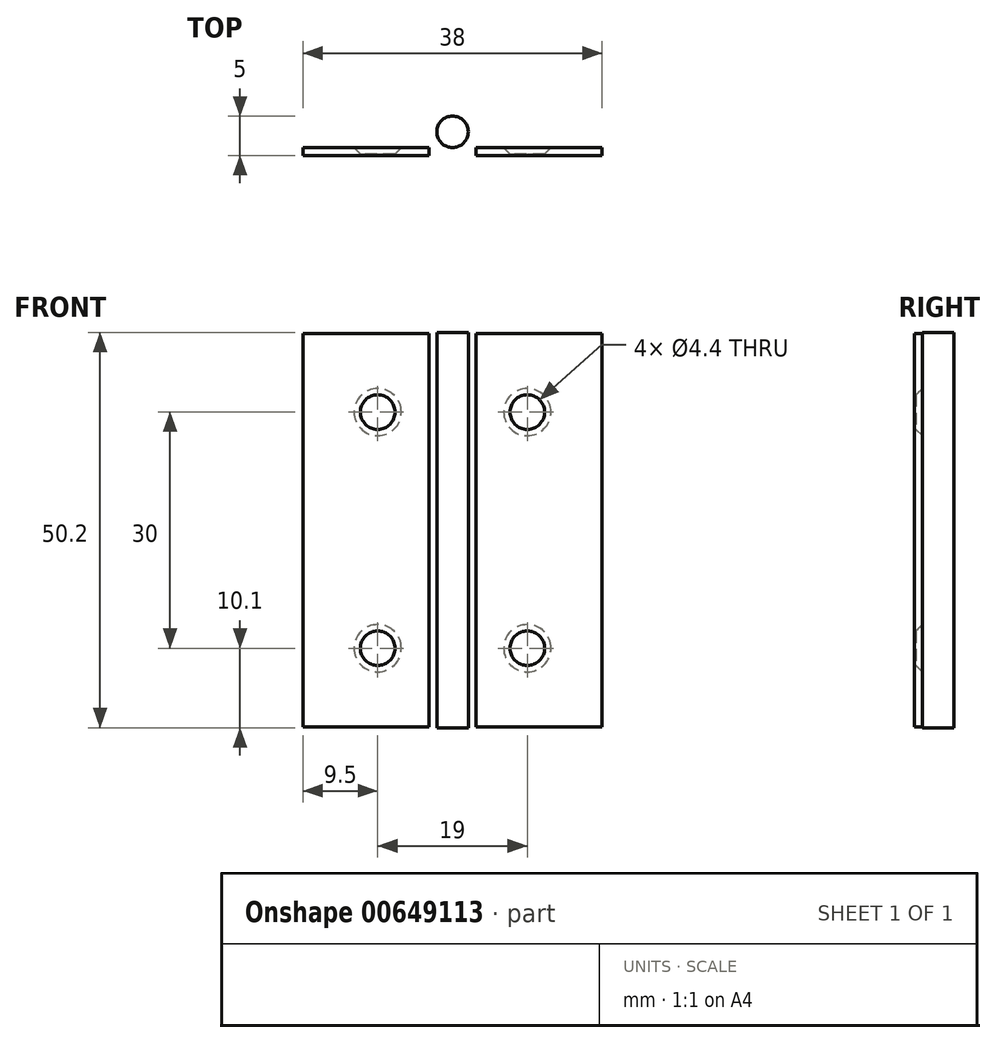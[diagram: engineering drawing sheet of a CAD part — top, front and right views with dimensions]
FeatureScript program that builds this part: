
annotation { "Feature Type Name" : "Feature", "Feature Type Description" : "" }
export const myFeature = defineFeature(function(context is Context, id is Id, definition is map)
    precondition{}
    {
        {
            var Q0;
            Q0=qCreatedBy(makeId("Top.planeOp"),FACE);
            var sketch = newSketch(context, id + "F0", { "sketchPlane" : qUnion([Q0])});
            skArc(sketch, "E0", {"start": v(0, -3) * mm, "mid": v(1.28, 2.71) * mm, "end": v(-2.32, -1.9) * mm});
            skLineSegment(sketch, "E1", {"start": v(0, -3) * mm, "end": v(-19, -3) * mm});
            skLineSegment(sketch, "E2", {"start": v(-19, -3) * mm, "end": v(-19, -2) * mm});
            skLineSegment(sketch, "E3", {"start": v(-19, -2) * mm, "end": v(0, -2) * mm});
            skArc(sketch, "E4.0", {"start": v(2.24, -2) * mm, "mid": v(0.07, 3) * mm, "end": v(-2.32, -1.9) * mm});
            skArc(sketch, "E5", {"start": v(0, -2) * mm, "mid": v(0.86, 1.8) * mm, "end": v(-1.55, -1.27) * mm});
            skLineSegment(sketch, "E6", {"start": v(-2.32, -1.9) * mm, "end": v(-1.55, -1.27) * mm});
            skSolve(sketch);
        }
        {
            var Q0;
            Q0=makeQuery(id+"F0.imprint","IMPRINT",FACE,{"disambiguationData":[TD([[makeQuery(id+"F0.imprint","IMPRINT",EDGE,{"derivedFrom":sQuery(id+"F0.wireOp",EDGE,"E0")}),1.0]])]});
            extrude(context, id + "F1", {"entities" : qUnion([Q0]), "oppositeDirection" : true, "depth" : 50 * mm, "offsetDistance" : 25 * mm});
        }
        {
            var Q0;
            Q0=qCreatedBy(makeId("Top.planeOp"),FACE);
            var sketch = newSketch(context, id + "F2", { "sketchPlane" : qUnion([Q0])});
            skLineSegment(sketch, "E7.MirrorCS", {"start": v(2.32, -1.9) * mm, "end": v(1.55, -1.27) * mm});
            skArc(sketch, "E8.MirrorCS", {"start": v(0, -2) * mm, "mid": v(-0.86, 1.8) * mm, "end": v(1.55, -1.27) * mm});
            skArc(sketch, "E9.MirrorCS", {"start": v(0, -3) * mm, "mid": v(-1.28, 2.71) * mm, "end": v(2.32, -1.9) * mm});
            skLineSegment(sketch, "E10.MirrorCS", {"start": v(19, -2) * mm, "end": v(0, -2) * mm});
            skLineSegment(sketch, "E11.MirrorCS", {"start": v(0, -3) * mm, "end": v(19, -3) * mm});
            skLineSegment(sketch, "E12.MirrorCS", {"start": v(19, -3) * mm, "end": v(19, -2) * mm});
            skSolve(sketch);
        }
        {
            var Q0;
            Q0=makeQuery(id+"F2.imprint","IMPRINT",FACE,{"disambiguationData":[TD([[makeQuery(id+"F2.imprint","IMPRINT",EDGE,{"derivedFrom":sQuery(id+"F2.wireOp",EDGE,"E7.MirrorCS")}),-1.0]])]});
            extrude(context, id + "F3", {"entities" : qUnion([Q0]), "oppositeDirection" : true, "depth" : 50 * mm, "offsetDistance" : 25 * mm});
        }
        {
            var Q0;
            Q0=qCreatedBy(makeId("Front.planeOp"),FACE);
            var sketch = newSketch(context, id + "F4", { "sketchPlane" : qUnion([Q0])});
            skLineSegment(sketch, "E13.bottom", {"start": v(-3, -50) * mm, "end": v(3, -50) * mm});
            skLineSegment(sketch, "E13.top", {"start": v(-3, -37.45) * mm, "end": v(3, -37.45) * mm});
            skLineSegment(sketch, "E13.left", {"start": v(-3, -50) * mm, "end": v(-3, -37.45) * mm});
            skLineSegment(sketch, "E13.right", {"start": v(3, -50) * mm, "end": v(3, -37.45) * mm});
            skLineSegment(sketch, "E14.0.1.0", {"start": v(3, -37.5) * mm, "end": v(3, -24.95) * mm});
            skLineSegment(sketch, "E14.0.1.1", {"start": v(-3, -37.5) * mm, "end": v(-3, -24.95) * mm});
            skLineSegment(sketch, "E14.0.1.2", {"start": v(-3, -24.95) * mm, "end": v(3, -24.95) * mm});
            skLineSegment(sketch, "E14.0.1.3", {"start": v(-3, -37.5) * mm, "end": v(3, -37.5) * mm});
            skLineSegment(sketch, "E14.0.2.0", {"start": v(3, -25) * mm, "end": v(3, -12.45) * mm});
            skLineSegment(sketch, "E14.0.2.1", {"start": v(-3, -25) * mm, "end": v(-3, -12.45) * mm});
            skLineSegment(sketch, "E14.0.2.2", {"start": v(-3, -12.45) * mm, "end": v(3, -12.45) * mm});
            skLineSegment(sketch, "E14.0.2.3", {"start": v(-3, -25) * mm, "end": v(3, -25) * mm});
            skLineSegment(sketch, "E14.0.3.0", {"start": v(3, -12.5) * mm, "end": v(3, 0.05) * mm});
            skLineSegment(sketch, "E14.0.3.1", {"start": v(-3, -12.5) * mm, "end": v(-3, 0.05) * mm});
            skLineSegment(sketch, "E14.0.3.2", {"start": v(-3, 0.05) * mm, "end": v(3, 0.05) * mm});
            skLineSegment(sketch, "E14.0.3.3", {"start": v(-3, -12.5) * mm, "end": v(3, -12.5) * mm});
            skLineSegment(sketch, "E14.direction1", {"start": v(-3, -50) * mm, "end": v(22, -50) * mm, "construction": true});
            skLineSegment(sketch, "E14.direction2", {"start": v(-3, -50) * mm, "end": v(-3, -37.5) * mm, "construction": true});
            skSolve(sketch);
        }
        {
            var Q0;
            Q0=makeQuery(id+"F4.imprint","IMPRINT",FACE,{"disambiguationData":[TD([[makeQuery(id+"F4.imprint","IMPRINT",EDGE,{"derivedFrom":sQuery(id+"F4.wireOp",EDGE,"E14.0.3.0")}),1.0]])]});
            var Q1;
            Q1=makeQuery(id+"F4.imprint","IMPRINT",FACE,{"disambiguationData":[TD([[makeQuery(id+"F4.imprint","IMPRINT",EDGE,{"derivedFrom":sQuery(id+"F4.wireOp",EDGE,"E14.0.1.0")}),1.0]])]});
            var Q2;
            {var subQ0=sQuery(id+"F4.wireOp",EDGE,"E14.0.1.2");Q2=makeQuery(id+"F4.imprint","IMPRINT",FACE,{"disambiguationData":[TD([[makeQuery(id+"F4.imprint","IMPRINT",EDGE,{"derivedFrom":subQ0}),-1.0]])]});}
            extrude(context, id + "F5", {"entities" : qUnion([Q0, Q1, Q2]), "operationType" : NewBodyOperationType.REMOVE, "endBound" : BoundingType.THROUGH_ALL, "oppositeDirection" : true, "depth" : 25 * mm, "offsetDistance" : 25 * mm, "hasSecondDirection" : true, "secondDirectionBound" : SecondDirectionBoundingType.THROUGH_ALL, "secondDirectionOppositeDirection" : false, "secondDirectionDepth" : 25 * mm});
        }
        {
            var Q0;
            Q0=makeQuery(id+"F4.imprint","IMPRINT",FACE,{"disambiguationData":[TD([[makeQuery(id+"F4.imprint","IMPRINT",EDGE,{"derivedFrom":sQuery(id+"F4.wireOp",EDGE,"E14.0.2.0")}),1.0]])]});
            var Q1;
            Q1=makeQuery(id+"F4.imprint","IMPRINT",FACE,{"disambiguationData":[TD([[makeQuery(id+"F4.imprint","IMPRINT",EDGE,{"derivedFrom":sQuery(id+"F4.wireOp",EDGE,"E13.bottom")}),1.0]])]});
            var Q2;
            {var subQ0=sQuery(id+"F4.wireOp",EDGE,"E14.0.2.2");Q2=makeQuery(id+"F4.imprint","IMPRINT",FACE,{"disambiguationData":[TD([[makeQuery(id+"F4.imprint","IMPRINT",EDGE,{"derivedFrom":subQ0}),-1.0]])]});}
            var Q3;
            {var subQ0=sQuery(id+"F4.wireOp",EDGE,"E13.top");Q3=makeQuery(id+"F4.imprint","IMPRINT",FACE,{"disambiguationData":[TD([[makeQuery(id+"F4.imprint","IMPRINT",EDGE,{"derivedFrom":subQ0}),-1.0]])]});}
            extrude(context, id + "F6", {"entities" : qUnion([Q0, Q1, Q2, Q3]), "operationType" : NewBodyOperationType.REMOVE, "endBound" : BoundingType.THROUGH_ALL, "oppositeDirection" : true, "depth" : 25 * mm, "offsetDistance" : 25 * mm, "hasSecondDirection" : true, "secondDirectionBound" : SecondDirectionBoundingType.THROUGH_ALL, "secondDirectionOppositeDirection" : false, "secondDirectionDepth" : 25 * mm});
        }
        {
            var Q0;
            Q0=qCreatedBy(makeId("Top.planeOp"),FACE);
            var sketch = newSketch(context, id + "F7", { "sketchPlane" : qUnion([Q0])});
            skCircle(sketch, "E15", {"center": v(0, 0) * mm, "radius": 2 * mm});
            skSolve(sketch);
        }
        {
            var Q0;
            Q0=makeQuery(id+"F7.imprint","IMPRINT",FACE,{"disambiguationData":[TD([[makeQuery(id+"F7.imprint","IMPRINT",EDGE,{"derivedFrom":sQuery(id+"F7.wireOp",EDGE,"E15")}),1.0]])]});
            extrude(context, id + "F8", {"entities" : qUnion([Q0]), "oppositeDirection" : true, "depth" : 50.1 * mm, "offsetDistance" : 25 * mm, "hasSecondDirection" : true, "secondDirectionOppositeDirection" : false, "secondDirectionDepth" : .1 * mm});
        }
        {
            var Q0;
            Q0=makeQuery(id+"F1.opExtrude","SWEPT_FACE",FACE,{"disambiguationData":[OSD([sQuery(id+"F0.wireOp",EDGE,"E3")])]});
            var sketch = newSketch(context, id + "F9", { "sketchPlane" : qUnion([Q0])});
            skPoint(sketch, "E16", {"position": v(9.5, -10) * mm});
            skPoint(sketch, "E17", {"position": v(9.5, -40) * mm});
            skPoint(sketch, "E18", {"position": v(-9.5, -40) * mm});
            skPoint(sketch, "E19", {"position": v(-9.5, -10) * mm});
            skSolve(sketch);
        }
        {
            var Q0;
            Q0=sQuery(id+"F9.wireOp",VERTEX,"E16");
            var Q1;
            Q1=sQuery(id+"F9.wireOp",VERTEX,"E17");
            var Q2;
            Q2=sQuery(id+"F9.wireOp",VERTEX,"E18");
            var Q3;
            Q3=sQuery(id+"F9.wireOp",VERTEX,"E19");
            var Q4;
            Q4=makeQuery(id+"F1.opExtrude","SWEPT_BODY",BODY,{"disambiguationData":[OSD([sQuery(id+"F0.wireOp",EDGE,"E0"),sQuery(id+"F0.wireOp",EDGE,"E1"),sQuery(id+"F0.wireOp",EDGE,"E2"),sQuery(id+"F0.wireOp",EDGE,"E3"),sQuery(id+"F0.wireOp",EDGE,"E4.0"),sQuery(id+"F0.wireOp",EDGE,"E5"),sQuery(id+"F0.wireOp",EDGE,"E6")])]});
            var Q5;
            Q5=makeQuery(id+"F3.opExtrude","SWEPT_BODY",BODY,{"disambiguationData":[OSD([sQuery(id+"F2.wireOp",EDGE,"E7.MirrorCS"),sQuery(id+"F2.wireOp",EDGE,"E8.MirrorCS"),sQuery(id+"F2.wireOp",EDGE,"E9.MirrorCS"),sQuery(id+"F2.wireOp",EDGE,"E10.MirrorCS"),sQuery(id+"F2.wireOp",EDGE,"E11.MirrorCS"),sQuery(id+"F2.wireOp",EDGE,"E12.MirrorCS")])]});
            hole(context, id + "F10", {"style" : HoleStyle.C_SINK, "endStyle" : HoleEndStyle.BLIND, "holeDiameter" : 4.4 * mm, "cSinkDiameter" : 6 * mm, "cSinkAngle" : 90 * degree, "majorDiameter" : 4 * mm, "holeDepth" : 10 * mm, "isTappedThrough" : true, "tappedDepth" : 7.9 * mm, "tapClearance" : 3, "locations" : qUnion([Q0, Q1, Q2, Q3]), "scope" : qUnion([Q4, Q5])});
        }
    });
